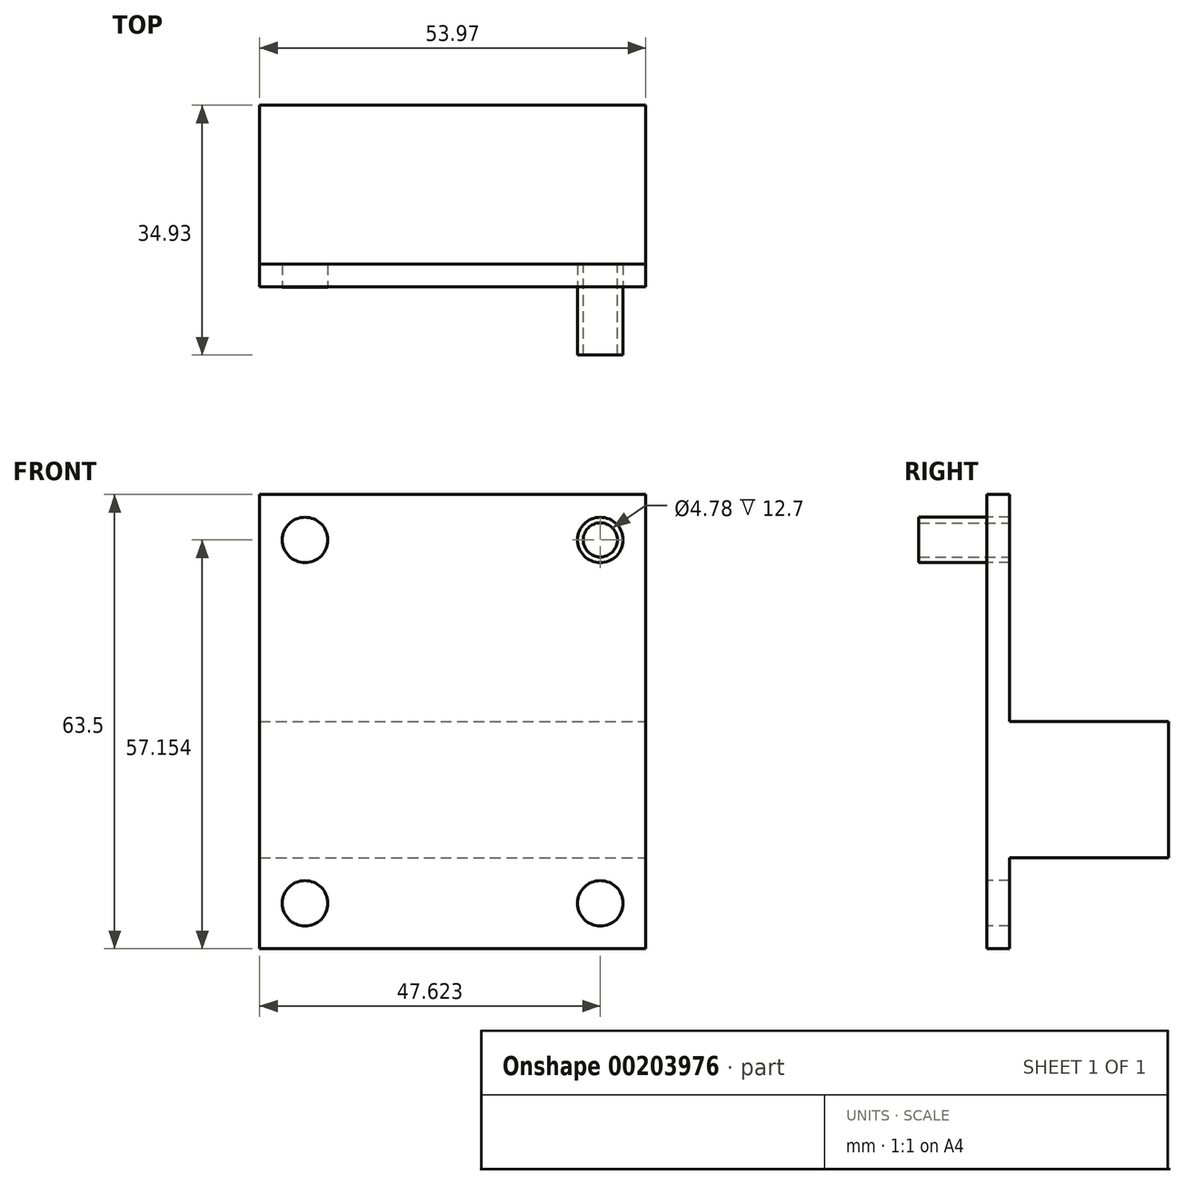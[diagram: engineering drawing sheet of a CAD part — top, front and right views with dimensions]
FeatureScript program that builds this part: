
annotation { "Feature Type Name" : "Feature", "Feature Type Description" : "" }
export const myFeature = defineFeature(function(context is Context, id is Id, definition is map)
    precondition{}
    {
        {
            var Q0;
            Q0=qCreatedBy(makeId("Front.planeOp"),FACE);
            var sketch = newSketch(context, id + "F0", { "sketchPlane" : qUnion([Q0])});
            skLineSegment(sketch, "E0.bottom", {"start": v(-34.6, -33.67) * mm, "end": v(19.37, -33.67) * mm});
            skLineSegment(sketch, "E0.top", {"start": v(-34.6, -46.37) * mm, "end": v(19.37, -46.37) * mm});
            skLineSegment(sketch, "E0.left", {"start": v(-34.6, -33.67) * mm, "end": v(-34.6, -46.37) * mm});
            skLineSegment(sketch, "E0.right", {"start": v(19.37, -33.67) * mm, "end": v(19.37, -46.37) * mm});
            skSolve(sketch);
        }
        {
            var Q0;
            Q0=makeQuery(id+"F0.imprint","IMPRINT",FACE,{"disambiguationData":[TD([[makeQuery(id+"F0.imprint","IMPRINT",EDGE,{"derivedFrom":sQuery(id+"F0.wireOp",EDGE,"E0.bottom")}),-1.0]])]});
            extrude(context, id + "F1", {"entities" : qUnion([Q0]), "depth" : 3.17 * mm});
        }
        {
            var Q0;
            Q0=makeQuery(id+"F1.opExtrude","CAP_FACE",FACE,{"disambiguationData":[OSD([sQuery(id+"F0.wireOp",EDGE,"E0.bottom"),sQuery(id+"F0.wireOp",EDGE,"E0.top"),sQuery(id+"F0.wireOp",EDGE,"E0.left"),sQuery(id+"F0.wireOp",EDGE,"E0.right")])],"isStart":false});
            var sketch = newSketch(context, id + "F2", { "sketchPlane" : qUnion([Q0])});
            skLineSegment(sketch, "E1", {"start": v(-34.6, -40.02) * mm, "end": v(-28.25, -40.02) * mm});
            skCircle(sketch, "E2", {"center": v(-28.25, -40.02) * mm, "radius": 3.18 * mm});
            skSolve(sketch);
        }
        {
            var Q0;
            Q0=makeQuery(id+"F2.imprint","IMPRINT",FACE,{"disambiguationData":[TD([[makeQuery(id+"F2.imprint","IMPRINT",EDGE,{"derivedFrom":sQuery(id+"F2.wireOp",EDGE,"E2")}),1.0]])]});
            extrude(context, id + "F3", {"entities" : qUnion([Q0]), "operationType" : NewBodyOperationType.ADD, "depth" : 3 / 203.2 * mm});
        }
        {
            var Q0;
            Q0=makeQuery(id+"F1.opExtrude","CAP_FACE",FACE,{"disambiguationData":[OSD([sQuery(id+"F0.wireOp",EDGE,"E0.bottom"),sQuery(id+"F0.wireOp",EDGE,"E0.top"),sQuery(id+"F0.wireOp",EDGE,"E0.left"),sQuery(id+"F0.wireOp",EDGE,"E0.right")])],"isStart":false});
            var sketch = newSketch(context, id + "F4", { "sketchPlane" : qUnion([Q0])});
            skLineSegment(sketch, "E3", {"start": v(19.37, -33.67) * mm, "end": v(19.37, -40.02) * mm});
            skLineSegment(sketch, "E4", {"start": v(19.37, -40.02) * mm, "end": v(13.02, -40.02) * mm});
            skCircle(sketch, "E5", {"center": v(13.02, -40.02) * mm, "radius": 3.18 * mm});
            skSolve(sketch);
        }
        {
            var Q0;
            Q0=makeQuery(id+"F4.imprint","IMPRINT",FACE,{"disambiguationData":[TD([[makeQuery(id+"F4.imprint","IMPRINT",EDGE,{"derivedFrom":sQuery(id+"F4.wireOp",EDGE,"E5")}),1.0]])]});
            var Q1;
            Q1=sQuery(id+"F4.wireOp",EDGE,"E5");
            extrude(context, id + "F5", {"entities" : qUnion([Q0]), "operationType" : NewBodyOperationType.REMOVE, "surfaceEntities" : qUnion([Q1]), "endBound" : BoundingType.THROUGH_ALL, "oppositeDirection" : true, "depth" : 25.4 * mm});
        }
        {
            var Q0;
            Q0=makeQuery(id+"F1.opExtrude","CAP_FACE",FACE,{"disambiguationData":[OSD([sQuery(id+"F0.wireOp",EDGE,"E0.bottom"),sQuery(id+"F0.wireOp",EDGE,"E0.top"),sQuery(id+"F0.wireOp",EDGE,"E0.left"),sQuery(id+"F0.wireOp",EDGE,"E0.right")])],"isStart":false});
            var sketch = newSketch(context, id + "F6", { "sketchPlane" : qUnion([Q0])});
            skLineSegment(sketch, "E6.bottom", {"start": v(-34.6, -33.67) * mm, "end": v(19.37, -33.67) * mm});
            skLineSegment(sketch, "E6.top", {"start": v(-34.6, -14.62) * mm, "end": v(19.37, -14.62) * mm});
            skLineSegment(sketch, "E6.left", {"start": v(-34.6, -33.67) * mm, "end": v(-34.6, -14.62) * mm});
            skLineSegment(sketch, "E6.right", {"start": v(19.37, -33.67) * mm, "end": v(19.37, -14.62) * mm});
            skSolve(sketch);
        }
        {
            var Q0;
            Q0=makeQuery(id+"F6.imprint","IMPRINT",FACE,{"disambiguationData":[TD([[makeQuery(id+"F6.imprint","IMPRINT",EDGE,{"derivedFrom":sQuery(id+"F6.wireOp",EDGE,"E6.bottom")}),1.0]])]});
            extrude(context, id + "F7", {"entities" : qUnion([Q0]), "operationType" : NewBodyOperationType.ADD, "oppositeDirection" : true, "depth" : 25.4 * mm});
        }
        {
            var Q0;
            Q0=makeQuery(id+"F7.boolean.opBoolean","MERGE",FACE,{"derivedFrom":[makeQuery(id+"F1.opExtrude","CAP_FACE",FACE,{"disambiguationData":[OSD([sQuery(id+"F0.wireOp",EDGE,"E0.bottom"),sQuery(id+"F0.wireOp",EDGE,"E0.top"),sQuery(id+"F0.wireOp",EDGE,"E0.left"),sQuery(id+"F0.wireOp",EDGE,"E0.right")])],"isStart":false}),makeQuery(id+"F7.opExtrude","CAP_FACE",FACE,{"disambiguationData":[OSD([sQuery(id+"F6.wireOp",EDGE,"E6.bottom"),sQuery(id+"F6.wireOp",EDGE,"E6.top"),sQuery(id+"F6.wireOp",EDGE,"E6.left"),sQuery(id+"F6.wireOp",EDGE,"E6.right")])],"isStart":true})]});
            var sketch = newSketch(context, id + "F8", { "sketchPlane" : qUnion([Q0])});
            skLineSegment(sketch, "E7.bottom", {"start": v(-34.6, -14.62) * mm, "end": v(19.37, -14.62) * mm});
            skLineSegment(sketch, "E7.top", {"start": v(-34.6, 17.13) * mm, "end": v(19.37, 17.13) * mm});
            skLineSegment(sketch, "E7.left", {"start": v(-34.6, -14.62) * mm, "end": v(-34.6, 17.13) * mm});
            skLineSegment(sketch, "E7.right", {"start": v(19.37, -14.62) * mm, "end": v(19.37, 17.13) * mm});
            skSolve(sketch);
        }
        {
            var Q0;
            Q0=makeQuery(id+"F8.imprint","IMPRINT",FACE,{"disambiguationData":[TD([[makeQuery(id+"F8.imprint","IMPRINT",EDGE,{"derivedFrom":sQuery(id+"F8.wireOp",EDGE,"E7.bottom")}),1.0]])]});
            extrude(context, id + "F9", {"entities" : qUnion([Q0]), "operationType" : NewBodyOperationType.ADD, "oppositeDirection" : true, "depth" : 3.17 * mm});
        }
        {
            var Q0;
            Q0=makeQuery(id+"F9.boolean.opBoolean","MERGE",FACE,{"derivedFrom":[makeQuery(id+"F7.boolean.opBoolean","MERGE",FACE,{"derivedFrom":[makeQuery(id+"F1.opExtrude","CAP_FACE",FACE,{"disambiguationData":[OSD([sQuery(id+"F0.wireOp",EDGE,"E0.bottom"),sQuery(id+"F0.wireOp",EDGE,"E0.top"),sQuery(id+"F0.wireOp",EDGE,"E0.left"),sQuery(id+"F0.wireOp",EDGE,"E0.right")])],"isStart":false}),makeQuery(id+"F7.opExtrude","CAP_FACE",FACE,{"disambiguationData":[OSD([sQuery(id+"F6.wireOp",EDGE,"E6.bottom"),sQuery(id+"F6.wireOp",EDGE,"E6.top"),sQuery(id+"F6.wireOp",EDGE,"E6.left"),sQuery(id+"F6.wireOp",EDGE,"E6.right")])],"isStart":true})]}),makeQuery(id+"F9.opExtrude","CAP_FACE",FACE,{"disambiguationData":[OSD([sQuery(id+"F8.wireOp",EDGE,"E7.bottom"),sQuery(id+"F8.wireOp",EDGE,"E7.top"),sQuery(id+"F8.wireOp",EDGE,"E7.left"),sQuery(id+"F8.wireOp",EDGE,"E7.right")])],"isStart":true})]});
            var sketch = newSketch(context, id + "F10", { "sketchPlane" : qUnion([Q0])});
            skLineSegment(sketch, "E8", {"start": v(-34.6, 17.13) * mm, "end": v(-34.6, 10.78) * mm});
            skLineSegment(sketch, "E9", {"start": v(-34.6, 10.78) * mm, "end": v(-28.25, 10.78) * mm});
            skCircle(sketch, "E10", {"center": v(-28.25, 10.78) * mm, "radius": 3.18 * mm});
            skSolve(sketch);
        }
        {
            var Q0;
            Q0=makeQuery(id+"F10.imprint","IMPRINT",FACE,{"disambiguationData":[TD([[makeQuery(id+"F10.imprint","IMPRINT",EDGE,{"derivedFrom":sQuery(id+"F10.wireOp",EDGE,"E10")}),1.0]])]});
            var Q1;
            Q1=sQuery(id+"F10.wireOp",EDGE,"E10");
            extrude(context, id + "F11", {"entities" : qUnion([Q0]), "operationType" : NewBodyOperationType.REMOVE, "surfaceEntities" : qUnion([Q1]), "endBound" : BoundingType.THROUGH_ALL, "oppositeDirection" : true, "depth" : 25.4 * mm});
        }
        {
            var Q0;
            Q0=makeQuery(id+"F9.boolean.opBoolean","MERGE",FACE,{"derivedFrom":[makeQuery(id+"F7.boolean.opBoolean","MERGE",FACE,{"derivedFrom":[makeQuery(id+"F1.opExtrude","CAP_FACE",FACE,{"disambiguationData":[OSD([sQuery(id+"F0.wireOp",EDGE,"E0.bottom"),sQuery(id+"F0.wireOp",EDGE,"E0.top"),sQuery(id+"F0.wireOp",EDGE,"E0.left"),sQuery(id+"F0.wireOp",EDGE,"E0.right")])],"isStart":false}),makeQuery(id+"F7.opExtrude","CAP_FACE",FACE,{"disambiguationData":[OSD([sQuery(id+"F6.wireOp",EDGE,"E6.bottom"),sQuery(id+"F6.wireOp",EDGE,"E6.top"),sQuery(id+"F6.wireOp",EDGE,"E6.left"),sQuery(id+"F6.wireOp",EDGE,"E6.right")])],"isStart":true})]}),makeQuery(id+"F9.opExtrude","CAP_FACE",FACE,{"disambiguationData":[OSD([sQuery(id+"F8.wireOp",EDGE,"E7.bottom"),sQuery(id+"F8.wireOp",EDGE,"E7.top"),sQuery(id+"F8.wireOp",EDGE,"E7.left"),sQuery(id+"F8.wireOp",EDGE,"E7.right")])],"isStart":true})]});
            var sketch = newSketch(context, id + "F12", { "sketchPlane" : qUnion([Q0])});
            skLineSegment(sketch, "E11", {"start": v(19.37, 17.13) * mm, "end": v(19.37, 10.78) * mm});
            skLineSegment(sketch, "E12", {"start": v(19.37, 10.78) * mm, "end": v(13.02, 10.78) * mm});
            skCircle(sketch, "E13", {"center": v(13.02, 10.78) * mm, "radius": 3.18 * mm});
            skSolve(sketch);
        }
        {
            var Q0;
            Q0=makeQuery(id+"F12.imprint","IMPRINT",FACE,{"disambiguationData":[TD([[makeQuery(id+"F12.imprint","IMPRINT",EDGE,{"derivedFrom":sQuery(id+"F12.wireOp",EDGE,"E13")}),1.0]])]});
            extrude(context, id + "F13", {"entities" : qUnion([Q0]), "operationType" : NewBodyOperationType.ADD, "depth" : 9.52 * mm});
        }
        {
            var Q0;
            Q0=makeQuery(id+"F9.opExtrude","CAP_FACE",FACE,{"disambiguationData":[OSD([sQuery(id+"F8.wireOp",EDGE,"E7.bottom"),sQuery(id+"F8.wireOp",EDGE,"E7.top"),sQuery(id+"F8.wireOp",EDGE,"E7.left"),sQuery(id+"F8.wireOp",EDGE,"E7.right")])],"isStart":false});
            var sketch = newSketch(context, id + "F14", { "sketchPlane" : qUnion([Q0])});
            skLineSegment(sketch, "E14", {"start": v(-19.37, 17.13) * mm, "end": v(-19.37, 10.78) * mm});
            skLineSegment(sketch, "E15", {"start": v(-19.37, 10.78) * mm, "end": v(-13.02, 10.78) * mm});
            skCircle(sketch, "E16", {"center": v(-13.02, 10.78) * mm, "radius": 2.39 * mm});
            skSolve(sketch);
        }
        {
            var Q0;
            Q0 = qSketchRegion(id + "F14", true);
            extrude(context, id + "F15", {"entities" : qUnion([Q0]), "operationType" : NewBodyOperationType.REMOVE, "oppositeDirection" : true, "depth" : 15.44 * mm});
        }
    });
